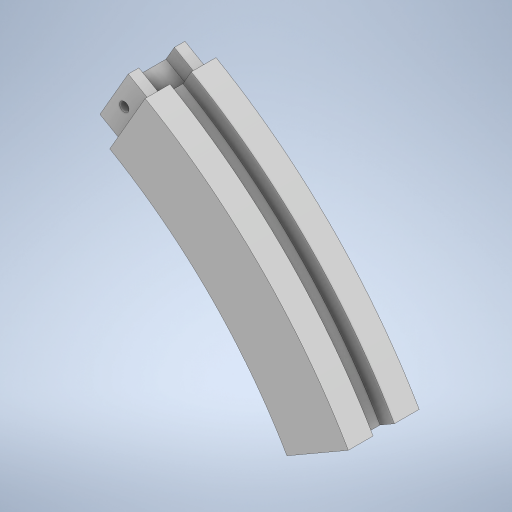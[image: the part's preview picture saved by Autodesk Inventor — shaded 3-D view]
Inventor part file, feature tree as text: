
AUTODESK INVENTOR PART (.ipt)
format: ipt  version: 2023 (Build 270158000, 158)  size: 396,800 bytes
history: native  units: mm
features: sketch x11, extrude x5, plane x4, loft x2, sweep x1
ambient origin geometry x8: Origin, YZ Plane, XZ Plane, XY Plane, X Axis, Y Axis, Z Axis, Center Point
bodies: Body1 (feature_tree)
feature tree (23):
  sweep  "Sweep2"
  extrude  "Extrusion3"  Depth=7.0mm
  extrude  "Extrusion4"  Depth=15.0mm
  sketch  "Sketch9"  dims[d41=220.0mm d42=60.0deg]
  plane  "Work Plane1"
  loft  "Loft1"
  plane  "Work Plane2"
  extrude  "Extrusion5"  TaperAngle=60.0deg  [1 undecoded]
  sketch  "Sketch12"  dims[d48=3.0mm d49=3.0mm]
  plane  "Work Plane3"
  loft  "Loft2"
  plane  "Work Plane4"
  extrude  "Extrusion6"  Depth=3.0mm
  extrude  "Extrusion7"  Depth=3.0mm
  sketch  "Sketch2"  dims[d5=100.0mm d18=9.0mm]
  sketch  "Sketch6"  dims[d19=7.0mm d21=16.0mm]
  sketch  "Sketch7"  dims[d22=30.0mm d23=15.0mm]
  sketch  "Sketch8"  dims[d24=4.5mm d25=8.0mm]
  sketch  "Sketch10"  dims[d43=220.0mm d44=0.0mm]
  sketch  "Sketch11"  dims[d45=0.0mm d46=0.0mm d47=3.0mm]
  sketch  "Sketch14"  dims[d50=3.0mm]
  sketch  "Sketch15"  dims[d51=3.0mm]
  sketch  "Sketch16"  dims[d52=3.0mm d53=3.0mm d54=3.0mm d55=3.0mm d56=10.0mm d57=0.0mm d58=4.0mm d59=12.0mm d60=5.0mm d61=0.0mm d62=0.0mm d63=80.0mm d64=80.0mm d65=40.0mm d66=40.0mm d67=50.0mm d68=30.0mm d69=9.6mm d70=15.0mm d71=31.0mm d72=0.0mm d73=90.0deg d74=0.0mm d75=90.0deg d76=-79.0mm d77=100.0mm d79=140.0mm d80=67.608902mm d81=140.0mm d82=150.0deg d83=50.0mm d84=0.0mm d85=0.0mm d86=5.0mm d87=10.0mm d88=10.0mm d89=10.0mm d90=10.0mm d91=-45.0mm d95=1.0mm d96=1.0mm d97=39.5mm d98=39.5mm d99=0.0mm d100=90.0deg d101=0.0mm d102=90.0deg d103=30.0mm d104=220.0mm d105=30.0deg d107=190.0mm d108=0.0mm d109=0.0mm d110=2.5mm d111=2.5mm d112=2.5mm d113=2.5mm d114=2.5mm d115=2.5mm d116=2.5mm d117=2.5mm d118=10.0mm d119=0.0mm]
note: 1 required parameter value undecoded (feature->parameter linkage not recoverable at this tier; creation-order binding heuristic only, values carry confidence <= 0.55)
